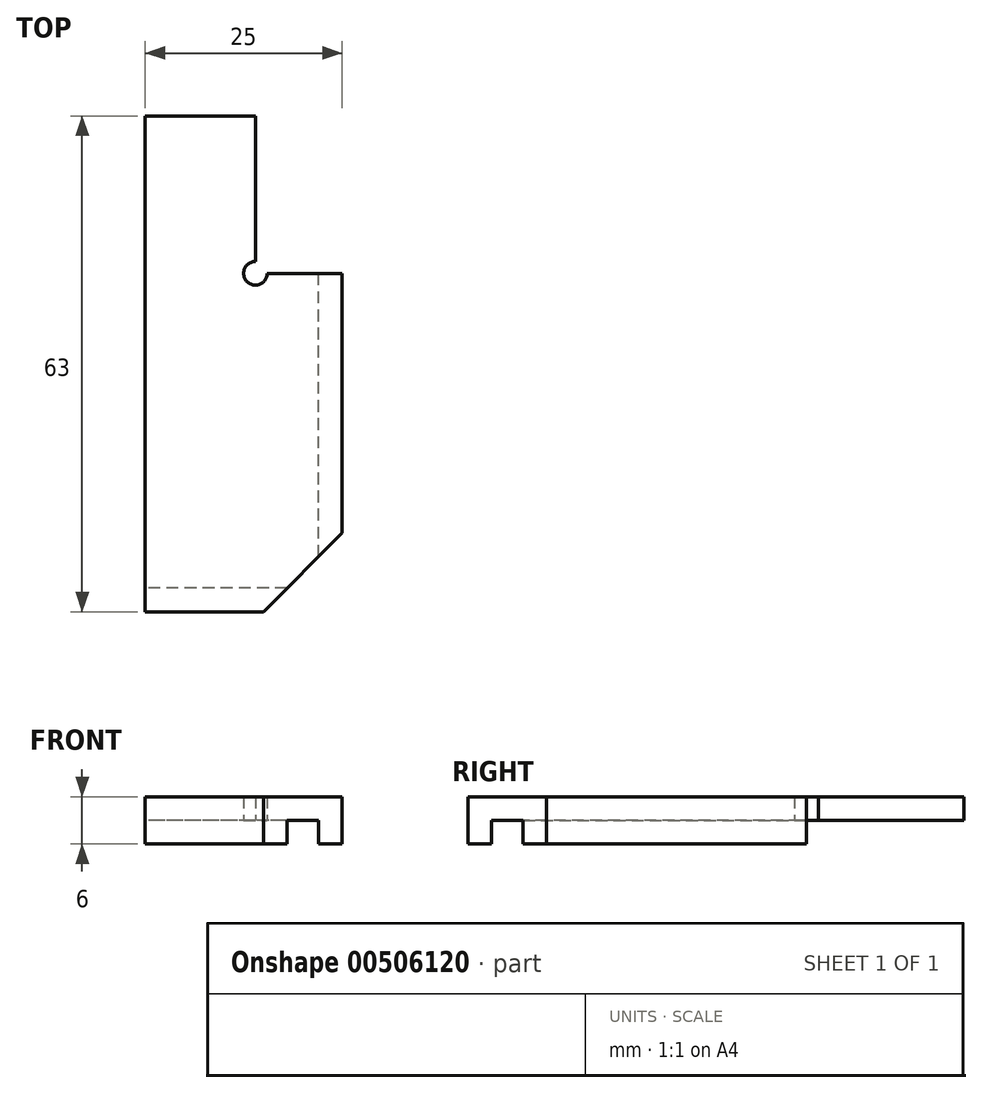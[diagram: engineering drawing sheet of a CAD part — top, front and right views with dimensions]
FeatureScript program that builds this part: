
annotation { "Feature Type Name" : "Feature", "Feature Type Description" : "" }
export const myFeature = defineFeature(function(context is Context, id is Id, definition is map)
    precondition{}
    {
        {
            var Q0;
            Q0=qCreatedBy(makeId("Top.planeOp"),FACE);
            var sketch = newSketch(context, id + "F0", { "sketchPlane" : qUnion([Q0])});
            skLineSegment(sketch, "E0", {"start": v(0, 0) * mm, "end": v(15, 0) * mm});
            skLineSegment(sketch, "E1", {"start": v(15, 0) * mm, "end": v(25, 10) * mm});
            skLineSegment(sketch, "E2", {"start": v(25, 10) * mm, "end": v(25, 43) * mm});
            skLineSegment(sketch, "E3", {"start": v(25, 43) * mm, "end": v(15.5, 43) * mm});
            skLineSegment(sketch, "E4", {"start": v(14, 44.5) * mm, "end": v(14, 63) * mm});
            skLineSegment(sketch, "E5", {"start": v(14, 63) * mm, "end": v(0, 63) * mm});
            skLineSegment(sketch, "E6", {"start": v(0, 63) * mm, "end": v(0, 0) * mm});
            skArc(sketch, "E7", {"start": v(14, 44.5) * mm, "mid": v(12.94, 41.94) * mm, "end": v(15.5, 43) * mm});
            skSolve(sketch);
        }
        {
            var Q0;
            Q0=qSketchRegion(id+"F0",true);
            extrude(context, id + "F1", {"entities" : qUnion([Q0]), "depth" : 3 * mm});
        }
        {
            var Q0;
            Q0=makeQuery(id+"F1.opExtrude","CAP_FACE",FACE,{"disambiguationData":[OSD([sQuery(id+"F0.wireOp",EDGE,"E0"),sQuery(id+"F0.wireOp",EDGE,"E1"),sQuery(id+"F0.wireOp",EDGE,"E2"),sQuery(id+"F0.wireOp",EDGE,"E3"),sQuery(id+"F0.wireOp",EDGE,"E4"),sQuery(id+"F0.wireOp",EDGE,"E5"),sQuery(id+"F0.wireOp",EDGE,"E6"),sQuery(id+"F0.wireOp",EDGE,"E7")])],"isStart":true});
            var sketch = newSketch(context, id + "F2", { "sketchPlane" : qUnion([Q0])});
            skLineSegment(sketch, "E8", {"start": v(0, 0) * mm, "end": v(15, 0) * mm});
            skLineSegment(sketch, "E9", {"start": v(15, 0) * mm, "end": v(18, -3) * mm});
            skLineSegment(sketch, "E10", {"start": v(18, -3) * mm, "end": v(0, -3) * mm});
            skLineSegment(sketch, "E11", {"start": v(0, -3) * mm, "end": v(0, 0) * mm});
            skLineSegment(sketch, "E12", {"start": v(25, -10) * mm, "end": v(22, -7) * mm});
            skLineSegment(sketch, "E13", {"start": v(22, -7) * mm, "end": v(22, -43) * mm});
            skLineSegment(sketch, "E14", {"start": v(22, -43) * mm, "end": v(25, -43) * mm});
            skLineSegment(sketch, "E15", {"start": v(25, -43) * mm, "end": v(25, -10) * mm});
            skSolve(sketch);
        }
        {
            var Q0;
            Q0=qSketchRegion(id+"F2",true);
            extrude(context, id + "F3", {"entities" : qUnion([Q0]), "operationType" : NewBodyOperationType.ADD, "depth" : 3 * mm});
        }
    });
